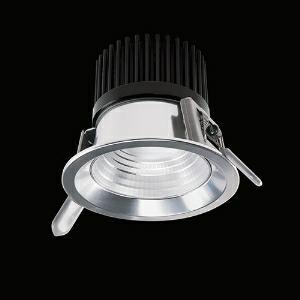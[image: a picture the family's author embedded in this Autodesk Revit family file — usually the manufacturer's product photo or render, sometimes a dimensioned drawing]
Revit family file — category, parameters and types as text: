
# Revit family: spectral_myral_myral_1500-830-s
name_source: partatom
category: Lighting Fixtures
revit_build: Autodesk Revit 2016 (Build: 20150220_1215(x64)
units: mm (PartAtom-declared; Revit-internal decimal feet)

## family parameters
Cut with Voids When Loaded = No
Host = Face
Light Source = No
Part Type = Normal
Room Calculation Point = No
Round Connector Dimension = Use Diameter
Shared = No

## types (1)
- SPECTRAL MYRAL (1 x )
    Apparent Load = 0 VA
    Approval mark = CE
    CIE Flux Codes = 85 100 100 100 100
    Control Gear = Electronic transformer
    Default Elevation = 1800 mm
    Description = SPG0320172
MYRAL recessed spot

Design:
    Height = 0 mm  [stored 0 ft]
    Lamp = 1 x
    Lamp count = 1
    Length = 120 mm
    Luminous efficacy = 0 lm/W
    Manufacturer = Ridi
    ModVariant = No
    Model = MYRAL 1500-830-S
    Mounting Place = Ceiling
    Mounting Type = Recessed
    Number of Poles = 1
    OnlyDefault = Yes
    Power Factor = 1
    Product Name = SPECTRAL MYRAL
    Product group = Downlight recessed
    ProductGroupID = 400
    Protection Class = Protection class
    Protection Degree = IP 20
    RlxData = <blob elided: 38917 chars, md5=332b84a6>
    Socket = socket
    Standby Power = 0 W
    System Light Flux = 0 lm
    System Power = 0 W
    Type Image = myral_04.jpg
    URL = http://reluxnet.relux.com
    VarID = ---
    Voltage = 0 V
    Weight = 0.00 kg
    Width = 0 mm  [stored 0 ft]

note: [stored X ft] marks values corroborated as IEEE doubles in the binary element streams (Revit-internal decimal feet)

## geometry (parser evidence)
native form markers: Sweep x9
no freeform markers — native parametric forms only
